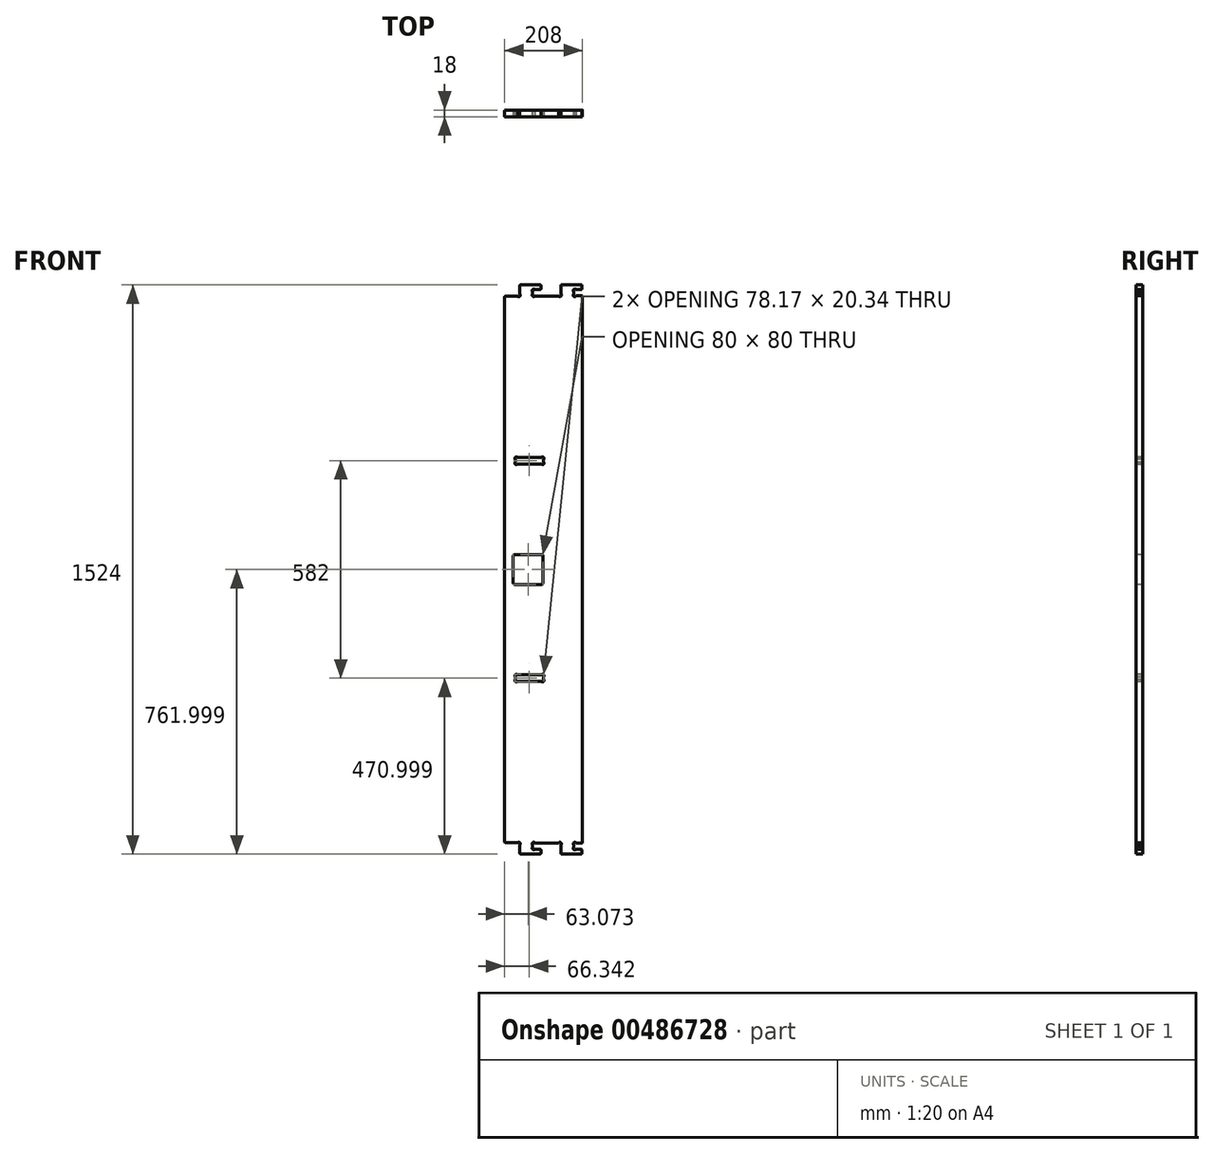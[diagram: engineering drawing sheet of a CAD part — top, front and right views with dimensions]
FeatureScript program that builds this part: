
annotation { "Feature Type Name" : "Feature", "Feature Type Description" : "" }
export const myFeature = defineFeature(function(context is Context, id is Id, definition is map)
    precondition{}
    {
        {
            var Q0;
            Q0=qCreatedBy(makeId("Front.planeOp"),FACE);
            var sketch = newSketch(context, id + "F0", { "sketchPlane" : qUnion([Q0])});
            skArc(sketch, "E0", {"start": v(-163.49, 53.85) * mm, "mid": v(-162.32, 56.68) * mm, "end": v(-159.49, 57.85) * mm});
            skLineSegment(sketch, "E1", {"start": v(-159.49, 57.85) * mm, "end": v(-87.49, 57.85) * mm});
            skArc(sketch, "E2", {"start": v(-87.49, 57.85) * mm, "mid": v(-84.66, 56.68) * mm, "end": v(-83.49, 53.85) * mm});
            skLineSegment(sketch, "E3", {"start": v(-83.49, 53.85) * mm, "end": v(-83.49, -18.15) * mm});
            skArc(sketch, "E4", {"start": v(-83.49, -18.15) * mm, "mid": v(-84.66, -20.98) * mm, "end": v(-87.49, -22.15) * mm});
            skLineSegment(sketch, "E5", {"start": v(-87.49, -22.15) * mm, "end": v(-159.49, -22.15) * mm});
            skArc(sketch, "E6", {"start": v(-159.49, -22.15) * mm, "mid": v(-162.32, -20.98) * mm, "end": v(-163.49, -18.15) * mm});
            skLineSegment(sketch, "E7", {"start": v(-163.49, -18.15) * mm, "end": v(-163.49, 53.85) * mm});
            skArc(sketch, "E8", {"start": v(-87.96, -282.15) * mm, "mid": v(-82.3, -282.15) * mm, "end": v(-82.3, -276.5) * mm});
            skLineSegment(sketch, "E9", {"start": v(-82.3, -276.5) * mm, "end": v(-82.3, -269.8) * mm});
            skArc(sketch, "E10", {"start": v(-82.3, -269.8) * mm, "mid": v(-82.3, -264.15) * mm, "end": v(-87.96, -264.15) * mm});
            skLineSegment(sketch, "E11", {"start": v(-87.96, -264.15) * mm, "end": v(-152.48, -264.15) * mm});
            skArc(sketch, "E12", {"start": v(-152.48, -264.15) * mm, "mid": v(-158.13, -264.15) * mm, "end": v(-158.13, -269.8) * mm});
            skLineSegment(sketch, "E13", {"start": v(-158.13, -269.8) * mm, "end": v(-158.13, -276.5) * mm});
            skArc(sketch, "E14", {"start": v(-158.13, -276.5) * mm, "mid": v(-158.13, -282.15) * mm, "end": v(-152.48, -282.15) * mm});
            skLineSegment(sketch, "E15", {"start": v(-152.48, -282.15) * mm, "end": v(-87.96, -282.15) * mm});
            skLineSegment(sketch, "E16", {"start": v(-82.3, 305.5) * mm, "end": v(-82.3, 312.2) * mm});
            skArc(sketch, "E17", {"start": v(-82.3, 312.2) * mm, "mid": v(-82.3, 317.85) * mm, "end": v(-87.96, 317.85) * mm});
            skLineSegment(sketch, "E18", {"start": v(-87.96, 317.85) * mm, "end": v(-152.48, 317.85) * mm});
            skArc(sketch, "E19", {"start": v(-152.48, 317.85) * mm, "mid": v(-158.13, 317.85) * mm, "end": v(-158.13, 312.2) * mm});
            skLineSegment(sketch, "E20", {"start": v(-158.13, 312.2) * mm, "end": v(-158.13, 305.5) * mm});
            skArc(sketch, "E21", {"start": v(-158.13, 305.5) * mm, "mid": v(-158.13, 299.85) * mm, "end": v(-152.48, 299.85) * mm});
            skLineSegment(sketch, "E22", {"start": v(-152.48, 299.85) * mm, "end": v(-87.96, 299.85) * mm});
            skArc(sketch, "E23", {"start": v(-87.96, 299.85) * mm, "mid": v(-82.3, 299.85) * mm, "end": v(-82.3, 305.5) * mm});
            skLineSegment(sketch, "E24", {"start": v(-105.9, -713.65) * mm, "end": v(-105.29, -714.15) * mm});
            skLineSegment(sketch, "E25", {"start": v(-105.29, -714.15) * mm, "end": v(-41.96, -714.15) * mm});
            skLineSegment(sketch, "E26", {"start": v(-41.96, -714.15) * mm, "end": v(-41.47, -713.65) * mm});
            skArc(sketch, "E27", {"start": v(-41.47, -713.65) * mm, "mid": v(-35.81, -713.65) * mm, "end": v(-35.81, -719.3) * mm});
            skLineSegment(sketch, "E28", {"start": v(-35.81, -719.3) * mm, "end": v(-35.8, -742.15) * mm});
            skArc(sketch, "E29", {"start": v(-35.8, -742.15) * mm, "mid": v(-35.22, -743.57) * mm, "end": v(-33.8, -744.15) * mm});
            skLineSegment(sketch, "E30", {"start": v(-33.8, -744.15) * mm, "end": v(18.44, -744.15) * mm});
            skArc(sketch, "E31", {"start": v(18.44, -744.15) * mm, "mid": v(19.85, -743.56) * mm, "end": v(20.44, -742.15) * mm});
            skLineSegment(sketch, "E32", {"start": v(20.44, -742.15) * mm, "end": v(20.44, -733.65) * mm});
            skArc(sketch, "E33", {"start": v(20.44, -733.65) * mm, "mid": v(19.85, -732.24) * mm, "end": v(18.44, -731.65) * mm});
            skLineSegment(sketch, "E34", {"start": v(18.44, -731.65) * mm, "end": v(4.1, -731.65) * mm});
            skArc(sketch, "E35", {"start": v(4.1, -731.65) * mm, "mid": v(-1.56, -731.65) * mm, "end": v(-1.56, -726) * mm});
            skLineSegment(sketch, "E36", {"start": v(-1.56, -726) * mm, "end": v(-1.56, -719.3) * mm});
            skArc(sketch, "E37", {"start": v(-1.56, -719.3) * mm, "mid": v(-1.56, -713.65) * mm, "end": v(4.1, -713.65) * mm});
            skLineSegment(sketch, "E38", {"start": v(4.1, -713.65) * mm, "end": v(5.07, -714.65) * mm});
            skLineSegment(sketch, "E39", {"start": v(5.07, -714.65) * mm, "end": v(20.44, -714.65) * mm});
            skArc(sketch, "E40", {"start": v(20.44, -714.65) * mm, "mid": v(21.14, -714.36) * mm, "end": v(21.44, -713.65) * mm});
            skLineSegment(sketch, "E41", {"start": v(21.44, -713.65) * mm, "end": v(21.44, 749.35) * mm});
            skArc(sketch, "E42", {"start": v(21.44, 749.35) * mm, "mid": v(21.14, 750.06) * mm, "end": v(20.44, 750.35) * mm});
            skLineSegment(sketch, "E43", {"start": v(20.44, 750.35) * mm, "end": v(5.12, 750.35) * mm});
            skLineSegment(sketch, "E44", {"start": v(5.12, 750.35) * mm, "end": v(4.1, 749.35) * mm});
            skArc(sketch, "E45", {"start": v(4.1, 749.35) * mm, "mid": v(-1.56, 749.35) * mm, "end": v(-1.56, 755) * mm});
            skLineSegment(sketch, "E46", {"start": v(-1.56, 755) * mm, "end": v(-1.56, 761.7) * mm});
            skArc(sketch, "E47", {"start": v(-1.56, 761.7) * mm, "mid": v(-1.56, 767.35) * mm, "end": v(4.1, 767.35) * mm});
            skLineSegment(sketch, "E48", {"start": v(4.1, 767.35) * mm, "end": v(18.44, 767.35) * mm});
            skArc(sketch, "E49", {"start": v(18.44, 767.35) * mm, "mid": v(19.85, 767.94) * mm, "end": v(20.44, 769.35) * mm});
            skLineSegment(sketch, "E50", {"start": v(20.44, 769.35) * mm, "end": v(20.44, 777.85) * mm});
            skArc(sketch, "E51", {"start": v(20.44, 777.85) * mm, "mid": v(19.85, 779.26) * mm, "end": v(18.44, 779.85) * mm});
            skLineSegment(sketch, "E52", {"start": v(18.44, 779.85) * mm, "end": v(-33.8, 779.85) * mm});
            skArc(sketch, "E53", {"start": v(-33.8, 779.85) * mm, "mid": v(-35.22, 779.26) * mm, "end": v(-35.8, 777.85) * mm});
            skLineSegment(sketch, "E54", {"start": v(-35.8, 777.85) * mm, "end": v(-35.81, 755) * mm});
            skArc(sketch, "E55", {"start": v(-35.81, 755) * mm, "mid": v(-35.81, 749.35) * mm, "end": v(-41.47, 749.35) * mm});
            skLineSegment(sketch, "E56", {"start": v(-41.47, 749.35) * mm, "end": v(-41.97, 749.85) * mm});
            skLineSegment(sketch, "E57", {"start": v(-41.97, 749.85) * mm, "end": v(-105.25, 749.85) * mm});
            skLineSegment(sketch, "E58", {"start": v(-105.25, 749.85) * mm, "end": v(-105.9, 749.35) * mm});
            skArc(sketch, "E59", {"start": v(-105.9, 749.35) * mm, "mid": v(-111.56, 749.35) * mm, "end": v(-111.56, 755) * mm});
            skLineSegment(sketch, "E60", {"start": v(-111.56, 755) * mm, "end": v(-111.56, 761.7) * mm});
            skArc(sketch, "E61", {"start": v(-111.56, 761.7) * mm, "mid": v(-111.56, 767.35) * mm, "end": v(-105.9, 767.35) * mm});
            skLineSegment(sketch, "E62", {"start": v(-105.9, 767.35) * mm, "end": v(-91.56, 767.35) * mm});
            skArc(sketch, "E63", {"start": v(-91.56, 767.35) * mm, "mid": v(-90.15, 767.94) * mm, "end": v(-89.56, 769.35) * mm});
            skLineSegment(sketch, "E64", {"start": v(-89.56, 769.35) * mm, "end": v(-89.56, 777.85) * mm});
            skArc(sketch, "E65", {"start": v(-89.56, 777.85) * mm, "mid": v(-90.15, 779.26) * mm, "end": v(-91.56, 779.85) * mm});
            skLineSegment(sketch, "E66", {"start": v(-91.56, 779.85) * mm, "end": v(-143.81, 779.85) * mm});
            skArc(sketch, "E67", {"start": v(-143.81, 779.85) * mm, "mid": v(-145.22, 779.26) * mm, "end": v(-145.81, 777.85) * mm});
            skLineSegment(sketch, "E68", {"start": v(-145.81, 777.85) * mm, "end": v(-145.81, 755) * mm});
            skArc(sketch, "E69", {"start": v(-145.81, 755) * mm, "mid": v(-145.81, 749.35) * mm, "end": v(-151.47, 749.35) * mm});
            skLineSegment(sketch, "E70", {"start": v(-151.47, 749.35) * mm, "end": v(-184.56, 749.35) * mm});
            skArc(sketch, "E71", {"start": v(-184.56, 749.35) * mm, "mid": v(-185.98, 748.76) * mm, "end": v(-186.56, 747.35) * mm});
            skLineSegment(sketch, "E72", {"start": v(-186.56, 747.35) * mm, "end": v(-186.56, -711.65) * mm});
            skArc(sketch, "E73", {"start": v(-186.56, -711.65) * mm, "mid": v(-185.98, -713.06) * mm, "end": v(-184.56, -713.65) * mm});
            skLineSegment(sketch, "E74", {"start": v(-184.56, -713.65) * mm, "end": v(-151.47, -713.65) * mm});
            skArc(sketch, "E75", {"start": v(-151.47, -713.65) * mm, "mid": v(-145.81, -713.65) * mm, "end": v(-145.81, -719.3) * mm});
            skLineSegment(sketch, "E76", {"start": v(-145.81, -719.3) * mm, "end": v(-145.81, -742.15) * mm});
            skArc(sketch, "E77", {"start": v(-145.81, -742.15) * mm, "mid": v(-145.22, -743.57) * mm, "end": v(-143.81, -744.15) * mm});
            skLineSegment(sketch, "E78", {"start": v(-143.81, -744.15) * mm, "end": v(-91.56, -744.15) * mm});
            skArc(sketch, "E79", {"start": v(-91.56, -744.15) * mm, "mid": v(-90.15, -743.56) * mm, "end": v(-89.56, -742.15) * mm});
            skLineSegment(sketch, "E80", {"start": v(-89.56, -742.15) * mm, "end": v(-89.56, -733.65) * mm});
            skArc(sketch, "E81", {"start": v(-89.56, -733.65) * mm, "mid": v(-90.15, -732.24) * mm, "end": v(-91.56, -731.65) * mm});
            skLineSegment(sketch, "E82", {"start": v(-91.56, -731.65) * mm, "end": v(-105.9, -731.65) * mm});
            skArc(sketch, "E83", {"start": v(-105.9, -731.65) * mm, "mid": v(-111.56, -731.65) * mm, "end": v(-111.56, -726) * mm});
            skLineSegment(sketch, "E84", {"start": v(-111.56, -726) * mm, "end": v(-111.56, -719.3) * mm});
            skArc(sketch, "E85", {"start": v(-111.56, -719.3) * mm, "mid": v(-111.56, -713.65) * mm, "end": v(-105.9, -713.65) * mm});
            skSolve(sketch);
        }
        {
            var Q0;
            Q0=qSketchRegion(id+"F0",true);
            extrude(context, id + "F1", {"entities" : qUnion([Q0]), "oppositeDirection" : true, "depth" : 18 * mm});
        }
    });
